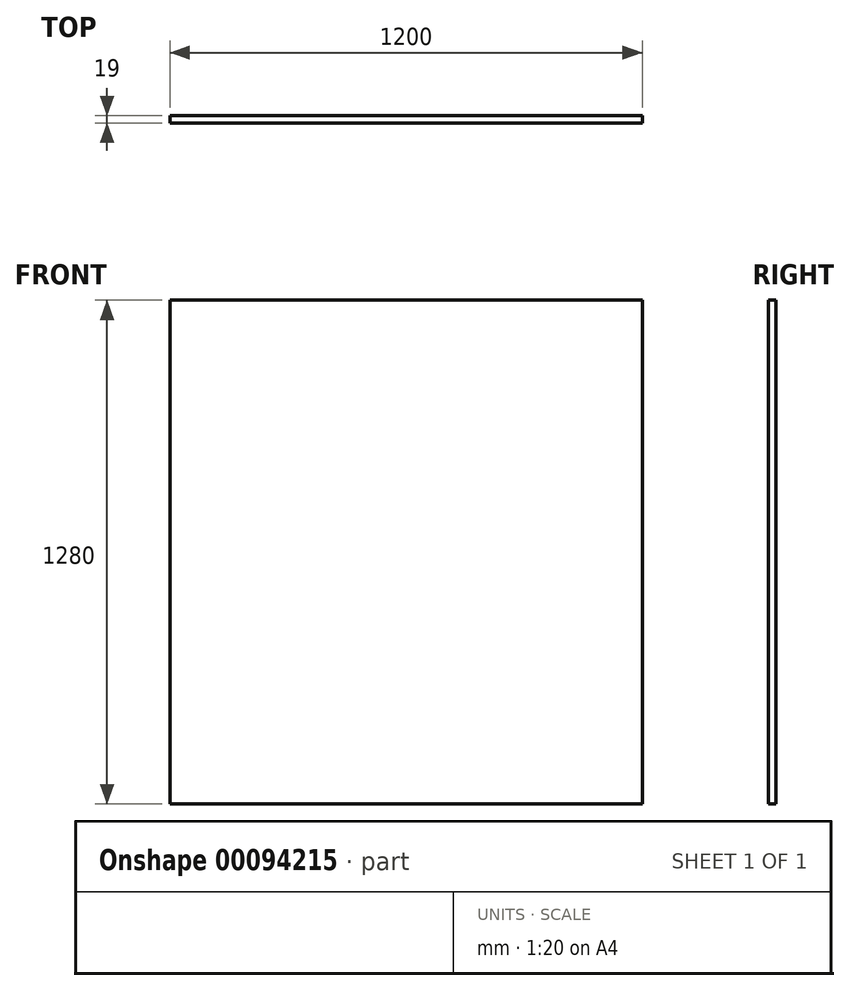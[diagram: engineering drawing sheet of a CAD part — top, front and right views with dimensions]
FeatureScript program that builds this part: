
annotation { "Feature Type Name" : "Feature", "Feature Type Description" : "" }
export const myFeature = defineFeature(function(context is Context, id is Id, definition is map)
    precondition{}
    {
        {
            var Q0;
            Q0=qCreatedBy(makeId("Front.planeOp"),FACE);
            var sketch = newSketch(context, id + "F0", { "sketchPlane" : qUnion([Q0])});
            skLineSegment(sketch, "E0.bottom", {"start": v(600, -1200) * mm, "end": v(-600, -1200) * mm});
            skLineSegment(sketch, "E0.top", {"start": v(600, 1200) * mm, "end": v(-600, 1200) * mm});
            skLineSegment(sketch, "E0.left", {"start": v(600, -1200) * mm, "end": v(600, 1200) * mm});
            skLineSegment(sketch, "E0.right", {"start": v(-600, -1200) * mm, "end": v(-600, 1200) * mm});
            skPoint(sketch, "E0.middle", {"position": v(0, 0) * mm});
            skLineSegment(sketch, "E1", {"start": v(-200, -1200) * mm, "end": v(-200, 80) * mm});
            skLineSegment(sketch, "E2", {"start": v(-600, 80) * mm, "end": v(-200, 80) * mm});
            skLineSegment(sketch, "E3", {"start": v(-200, 80) * mm, "end": v(600, 80) * mm});
            skLineSegment(sketch, "E4", {"start": v(200, 80) * mm, "end": v(200, -1200) * mm});
            skSolve(sketch);
        }
        {
            var Q0;
            Q0=makeQuery(id+"F0.imprint","IMPRINT",FACE,{"disambiguationData":[TD([[makeQuery(id+"F0.imprint","IMPRINT",EDGE,{"derivedFrom":sQuery(id+"F0.wireOp",EDGE,"E0.bottom")}),-1.0]])]});
            extrude(context, id + "F1", {"entities" : qUnion([Q0]), "endBound" : BoundingType.SYMMETRIC, "depth" : 19 * mm});
        }
    });
